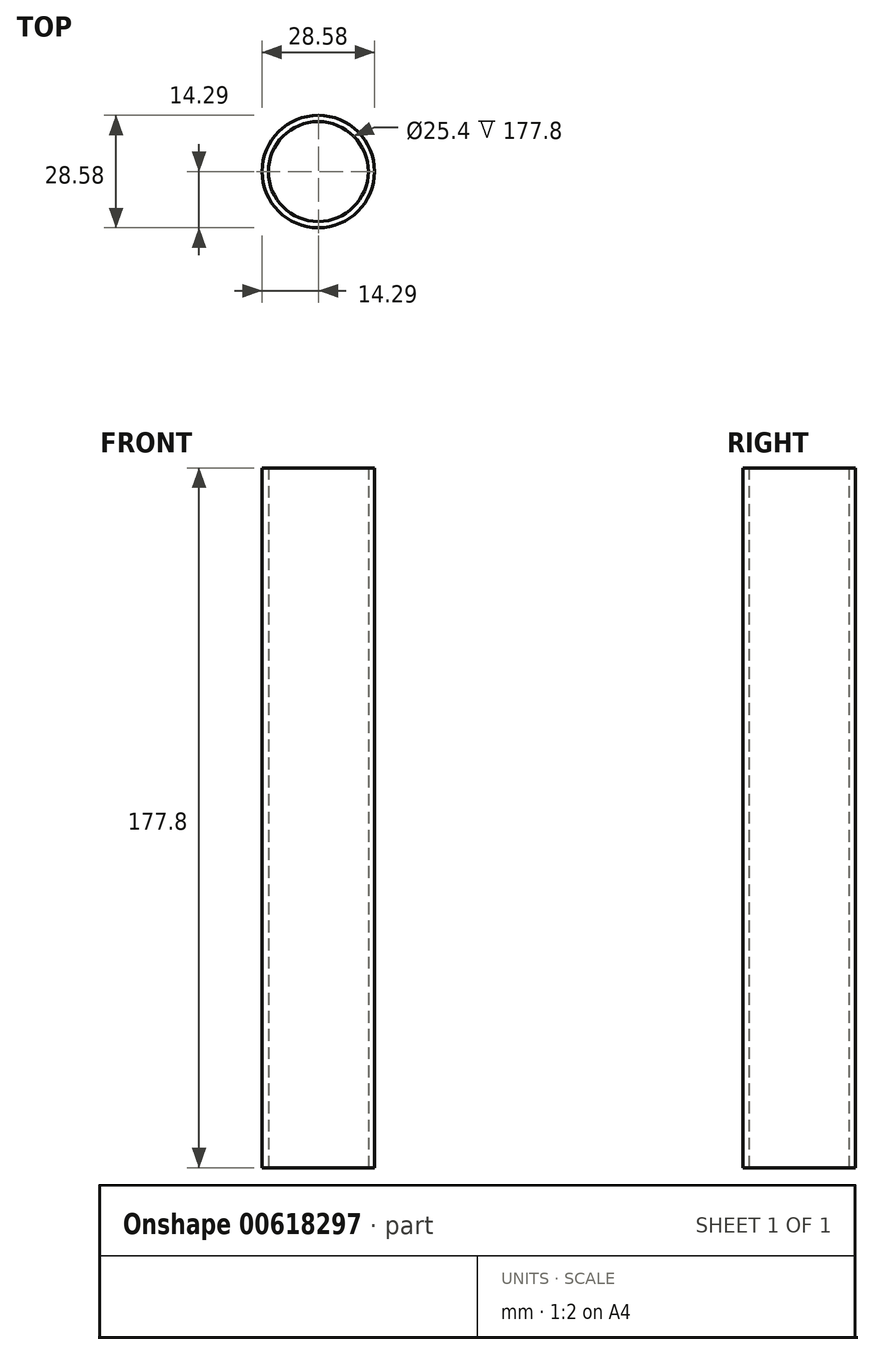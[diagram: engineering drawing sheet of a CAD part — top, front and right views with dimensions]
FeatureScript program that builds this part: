
annotation { "Feature Type Name" : "Feature", "Feature Type Description" : "" }
export const myFeature = defineFeature(function(context is Context, id is Id, definition is map)
    precondition{}
    {
        {
            var Q0;
            Q0=qCreatedBy(makeId("Top.planeOp"),FACE);
            var sketch = newSketch(context, id + "F0", { "sketchPlane" : qUnion([Q0])});
            skLineSegment(sketch, "E0", {"start": v(0, 0) * mm, "end": v(12.7, 0) * mm});
            skCircle(sketch, "E1", {"center": v(0, 0) * mm, "radius": 12.7 * mm});
            skCircle(sketch, "E2.0", {"center": v(0, 0) * mm, "radius": 14.29 * mm});
            skSolve(sketch);
        }
        {
            var Q0;
            Q0=qSketchRegion(id+"FEloJnSHgHgsXCt_0",true);
            var Q1;
            Q1=makeQuery(id+"F0.imprint","IMPRINT",FACE,{"disambiguationData":[TD([[makeQuery(id+"F0.imprint","IMPRINT",EDGE,{"derivedFrom":sQuery(id+"F0.wireOp",EDGE,"E1")}),-1.0]])]});
            extrude(context, id + "F1", {"entities" : qUnion([Q0, Q1]), "depth" : 177.8 * mm, "offsetDistance" : 25.4 * mm});
        }
    });
